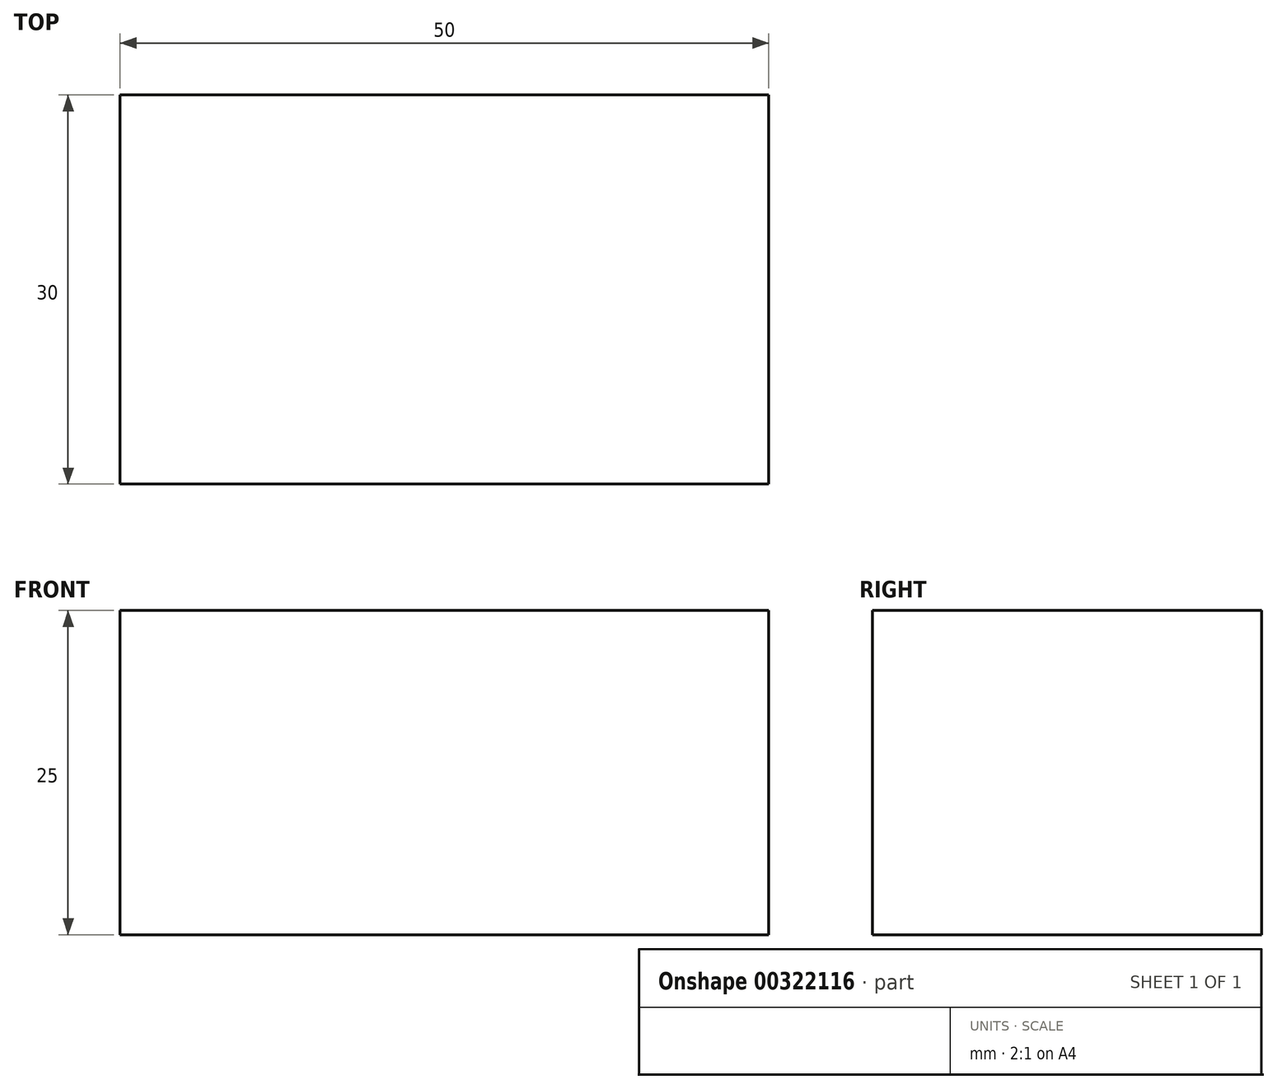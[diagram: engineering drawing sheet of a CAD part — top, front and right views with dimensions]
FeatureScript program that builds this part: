
annotation { "Feature Type Name" : "Feature", "Feature Type Description" : "" }
export const myFeature = defineFeature(function(context is Context, id is Id, definition is map)
    precondition{}
    {
        {
            var Q0;
            Q0=qCreatedBy(makeId("Top.planeOp"),FACE);
            var sketch = newSketch(context, id + "F0", { "sketchPlane" : qUnion([Q0])});
            skLineSegment(sketch, "E0.bottom", {"start": v(0, 0) * mm, "end": v(50, 0) * mm});
            skLineSegment(sketch, "E0.top", {"start": v(0, 30) * mm, "end": v(50, 30) * mm});
            skLineSegment(sketch, "E0.left", {"start": v(0, 0) * mm, "end": v(0, 30) * mm});
            skLineSegment(sketch, "E0.right", {"start": v(50, 0) * mm, "end": v(50, 30) * mm});
            skSolve(sketch);
        }
        {
            var Q0;
            Q0 = qSketchRegion(id + "F0", true);
            extrude(context, id + "F1", {"entities" : qUnion([Q0]), "depth" : 25 * mm});
        }
    });
